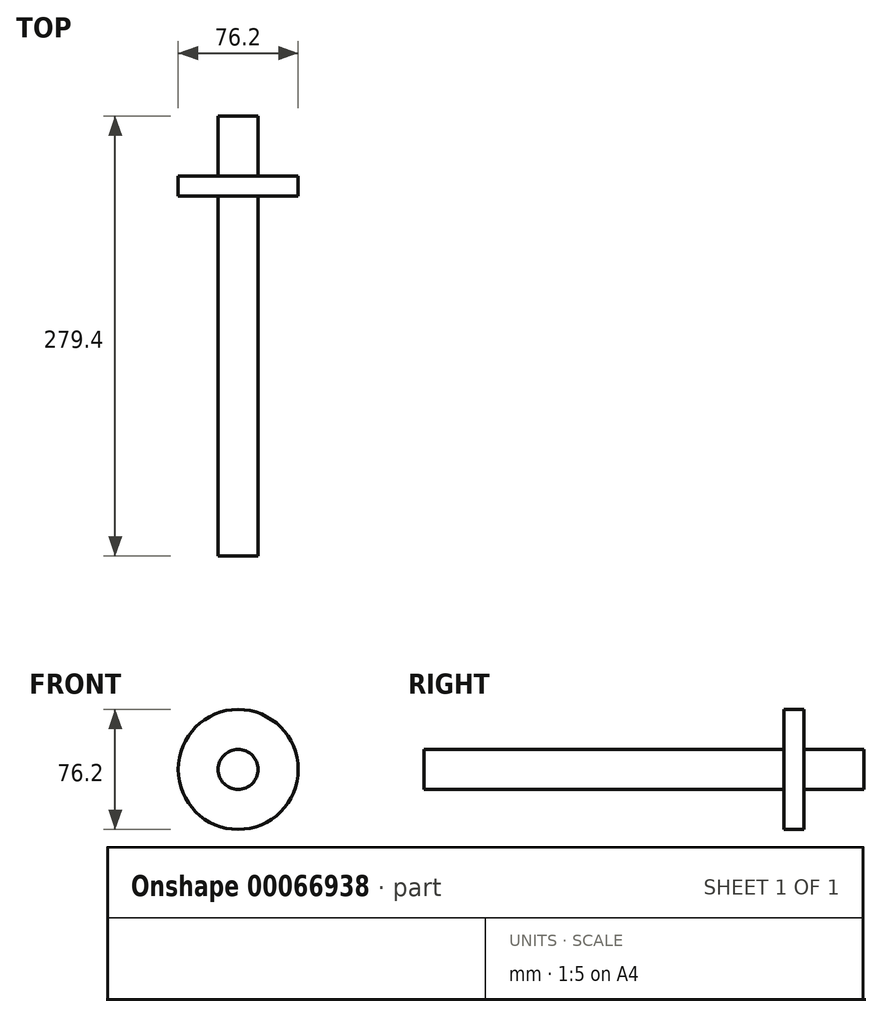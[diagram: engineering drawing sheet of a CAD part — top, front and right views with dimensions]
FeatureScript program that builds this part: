
annotation { "Feature Type Name" : "Feature", "Feature Type Description" : "" }
export const myFeature = defineFeature(function(context is Context, id is Id, definition is map)
    precondition{}
    {
        {
            var Q0;
            Q0=qCreatedBy(makeId("Front.planeOp"),FACE);
            var sketch = newSketch(context, id + "F0", { "sketchPlane" : qUnion([Q0])});
            skCircle(sketch, "E0", {"center": v(0, 0) * mm, "radius": 38.1 * mm});
            skSolve(sketch);
        }
        {
            var Q0;
            Q0=qSketchRegion(id+"F0",true);
            extrude(context, id + "F1", {"entities" : qUnion([Q0]), "depth" : 12.7 * mm});
        }
        {
            var Q0;
            Q0=makeQuery(id+"F1.opExtrude","CAP_FACE",FACE,{"disambiguationData":[OSD([sQuery(id+"F0.wireOp",EDGE,"E0")])],"isStart":false});
            var sketch = newSketch(context, id + "F2", { "sketchPlane" : qUnion([Q0])});
            skCircle(sketch, "E1", {"center": v(0, 0) * mm, "radius": 12.7 * mm});
            skSolve(sketch);
        }
        {
            var Q0;
            Q0=qSketchRegion(id+"F2",true);
            extrude(context, id + "F3", {"entities" : qUnion([Q0]), "operationType" : NewBodyOperationType.ADD, "depth" : 228.6 * mm});
        }
        {
            var Q0;
            Q0=makeQuery(id+"F1.opExtrude","CAP_FACE",FACE,{"disambiguationData":[OSD([sQuery(id+"F0.wireOp",EDGE,"E0")])],"isStart":true});
            var sketch = newSketch(context, id + "F4", { "sketchPlane" : qUnion([Q0])});
            skCircle(sketch, "E2", {"center": v(0, 0) * mm, "radius": 12.7 * mm});
            skSolve(sketch);
        }
        {
            var Q0;
            Q0=qSketchRegion(id+"F4",true);
            extrude(context, id + "F5", {"entities" : qUnion([Q0]), "operationType" : NewBodyOperationType.ADD, "depth" : 38.1 * mm});
        }
    });
